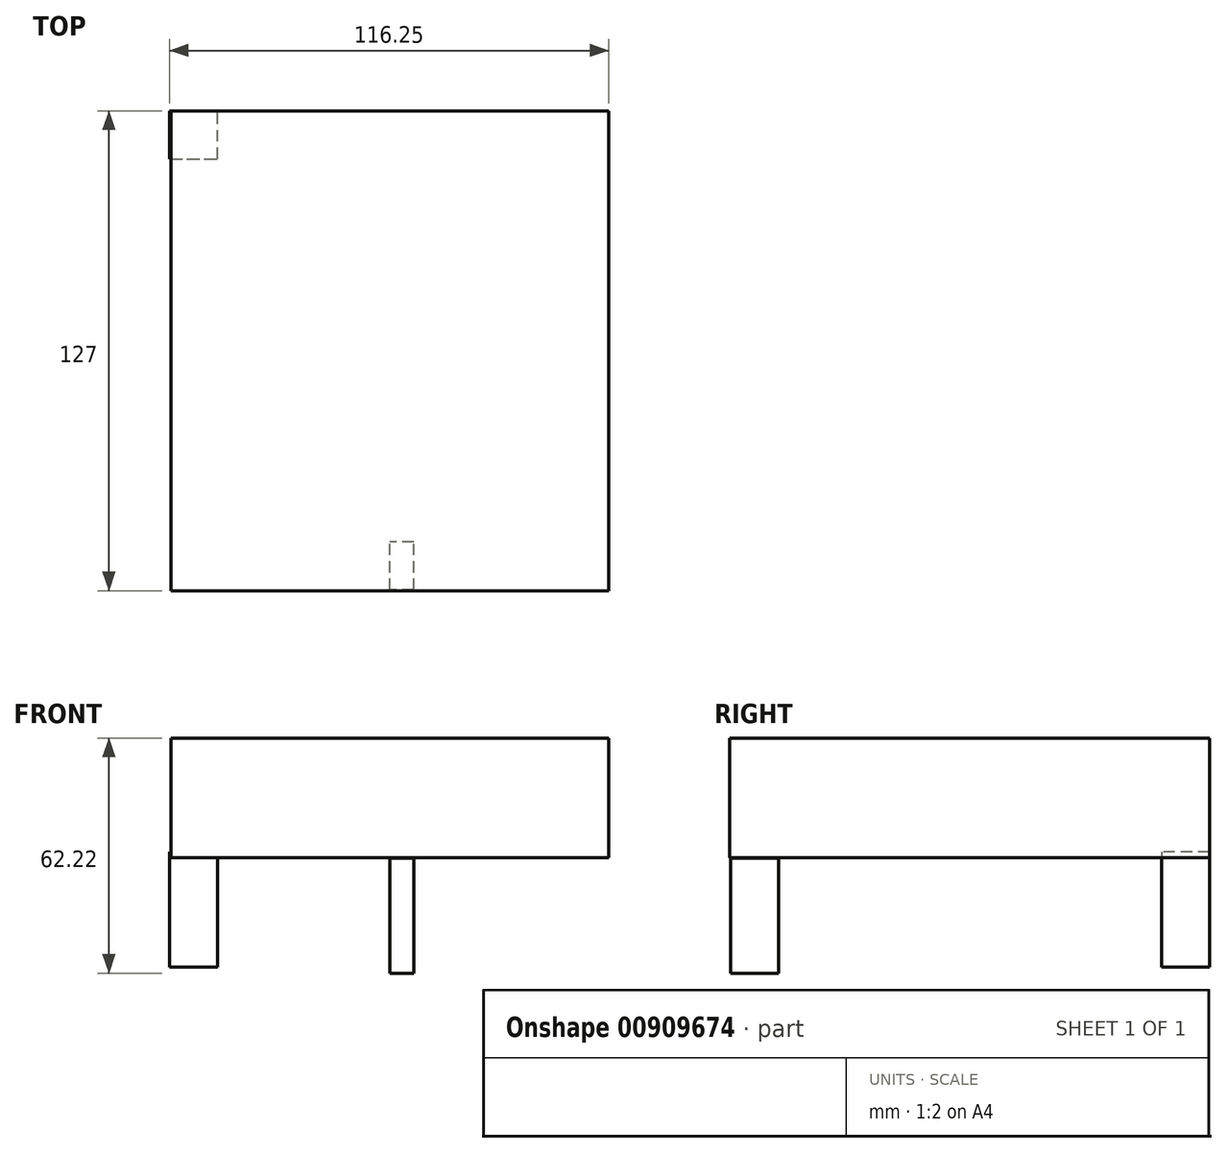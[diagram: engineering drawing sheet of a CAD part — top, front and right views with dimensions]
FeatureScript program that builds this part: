
annotation { "Feature Type Name" : "Feature", "Feature Type Description" : "" }
export const myFeature = defineFeature(function(context is Context, id is Id, definition is map)
    precondition{}
    {
        {
            var Q0;
            Q0=qCreatedBy(makeId("Front.planeOp"),FACE);
            var sketch = newSketch(context, id + "F0", { "sketchPlane" : qUnion([Q0])});
            skLineSegment(sketch, "E0.bottom", {"start": v(-57.9, 15.84) * mm, "end": v(57.9, 15.84) * mm});
            skLineSegment(sketch, "E0.top", {"start": v(-57.9, -15.84) * mm, "end": v(57.9, -15.84) * mm});
            skLineSegment(sketch, "E0.left", {"start": v(-57.9, 15.84) * mm, "end": v(-57.9, -15.84) * mm});
            skLineSegment(sketch, "E0.right", {"start": v(57.9, 15.84) * mm, "end": v(57.9, -15.84) * mm});
            skPoint(sketch, "E0.middle", {"position": v(0, 0) * mm});
            skSolve(sketch);
        }
        {
            var Q0;
            Q0 = qSketchRegion(id + "F0", true);
            extrude(context, id + "F1", {"entities" : qUnion([Q0]), "depth" : 127 * mm, "offsetDistance" : 25.4 * mm});
        }
        {
            var Q0;
            Q0=qCreatedBy(makeId("Right.planeOp"),FACE);
            var sketch = newSketch(context, id + "F2", { "sketchPlane" : qUnion([Q0])});
            skLineSegment(sketch, "E1.bottom", {"start": v(-126.78, -15.9) * mm, "end": v(-114.08, -15.9) * mm});
            skLineSegment(sketch, "E1.top", {"start": v(-126.78, -46.38) * mm, "end": v(-114.08, -46.38) * mm});
            skLineSegment(sketch, "E1.left", {"start": v(-126.78, -15.9) * mm, "end": v(-126.78, -46.38) * mm});
            skLineSegment(sketch, "E1.right", {"start": v(-114.08, -15.9) * mm, "end": v(-114.08, -46.38) * mm});
            skSolve(sketch);
        }
        {
            var Q0;
            Q0 = qSketchRegion(id + "F2", true);
            extrude(context, id + "F3", {"entities" : qUnion([Q0]), "depth" : 6.35 * mm, "offsetDistance" : 25.4 * mm});
        }
        {
            var Q0;
            Q0=qCreatedBy(makeId("Front.planeOp"),FACE);
            var sketch = newSketch(context, id + "F4", { "sketchPlane" : qUnion([Q0])});
            skLineSegment(sketch, "E2.bottom", {"start": v(-58.35, -14.36) * mm, "end": v(-45.65, -14.36) * mm});
            skLineSegment(sketch, "E2.top", {"start": v(-58.35, -44.84) * mm, "end": v(-45.65, -44.84) * mm});
            skLineSegment(sketch, "E2.left", {"start": v(-58.35, -14.36) * mm, "end": v(-58.35, -44.84) * mm});
            skLineSegment(sketch, "E2.right", {"start": v(-45.65, -14.36) * mm, "end": v(-45.65, -44.84) * mm});
            skSolve(sketch);
        }
        {
            var Q0;
            Q0=makeQuery(id+"F4.imprint","IMPRINT",FACE,{"disambiguationData":[TD([[makeQuery(id+"F4.imprint","IMPRINT",EDGE,{"derivedFrom":sQuery(id+"F4.wireOp",EDGE,"E2.bottom")}),-1.0]])]});
            extrude(context, id + "F5", {"entities" : qUnion([Q0]), "operationType" : NewBodyOperationType.ADD, "depth" : 12.7 * mm, "offsetDistance" : 25.4 * mm});
        }
    });
